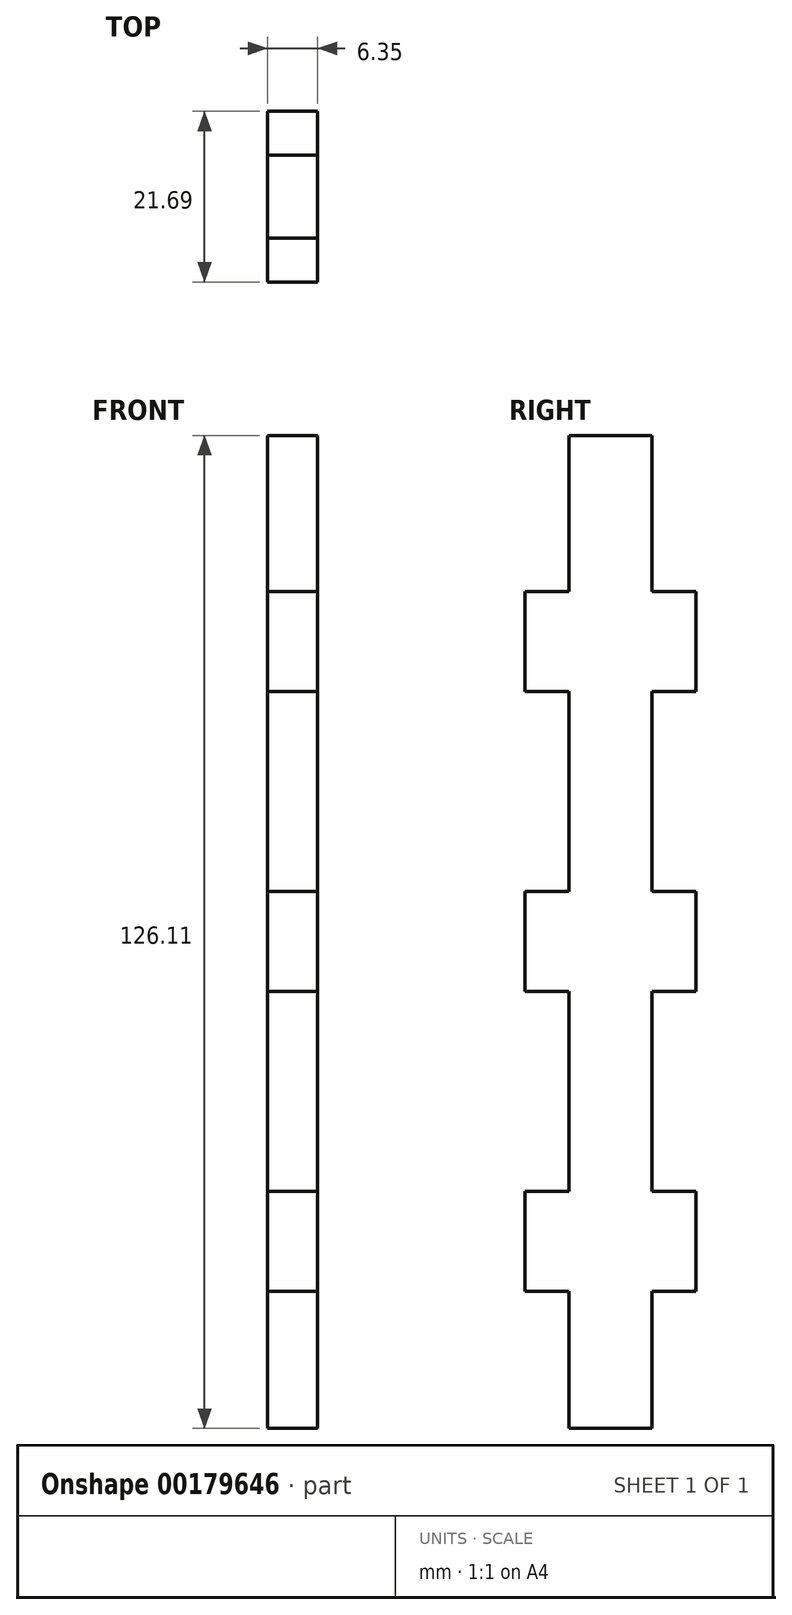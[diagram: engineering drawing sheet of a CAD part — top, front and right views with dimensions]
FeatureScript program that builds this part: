
annotation { "Feature Type Name" : "Feature", "Feature Type Description" : "" }
export const myFeature = defineFeature(function(context is Context, id is Id, definition is map)
    precondition{}
    {
        {
            var Q0;
            Q0=qCreatedBy(makeId("Right.planeOp"),FACE);
            var sketch = newSketch(context, id + "F0", { "sketchPlane" : qUnion([Q0])});
            skLineSegment(sketch, "E0.bottom", {"start": v(-44.05, 64.26) * mm, "end": v(-33.54, 64.26) * mm});
            skLineSegment(sketch, "E0.top", {"start": v(-44.05, -61.85) * mm, "end": v(-33.54, -61.85) * mm});
            skLineSegment(sketch, "E0.left", {"start": v(-49.64, 44.45) * mm, "end": v(-49.64, 31.75) * mm});
            skLineSegment(sketch, "E0.right", {"start": v(-27.95, 44.45) * mm, "end": v(-27.95, 31.75) * mm});
            skLineSegment(sketch, "E1", {"start": v(-33.54, 64.26) * mm, "end": v(-33.54, 44.45) * mm});
            skLineSegment(sketch, "E2", {"start": v(-33.54, 44.45) * mm, "end": v(-27.95, 44.45) * mm});
            skLineSegment(sketch, "E3", {"start": v(-27.95, 31.75) * mm, "end": v(-33.54, 31.75) * mm});
            skLineSegment(sketch, "E4", {"start": v(-33.54, 31.75) * mm, "end": v(-33.54, 6.35) * mm});
            skLineSegment(sketch, "E5", {"start": v(-33.54, 6.35) * mm, "end": v(-27.95, 6.35) * mm});
            skLineSegment(sketch, "E6", {"start": v(-27.95, 6.35) * mm, "end": v(-27.95, -6.35) * mm});
            skLineSegment(sketch, "E7", {"start": v(-27.95, -6.35) * mm, "end": v(-33.54, -6.35) * mm});
            skLineSegment(sketch, "E8", {"start": v(-33.54, -6.35) * mm, "end": v(-33.54, -31.75) * mm});
            skLineSegment(sketch, "E9", {"start": v(-33.54, -31.75) * mm, "end": v(-27.95, -31.75) * mm});
            skLineSegment(sketch, "E10", {"start": v(-27.95, -31.75) * mm, "end": v(-27.95, -44.45) * mm});
            skLineSegment(sketch, "E11", {"start": v(-27.95, -44.45) * mm, "end": v(-33.54, -44.45) * mm});
            skLineSegment(sketch, "E12", {"start": v(-33.54, -44.45) * mm, "end": v(-33.54, -61.85) * mm});
            skLineSegment(sketch, "E13.MirrorCS", {"start": v(-44.05, 64.26) * mm, "end": v(-44.05, 44.45) * mm});
            skLineSegment(sketch, "E14.MirrorCS", {"start": v(-44.05, 44.45) * mm, "end": v(-49.64, 44.45) * mm});
            skLineSegment(sketch, "E15.MirrorCS", {"start": v(-49.64, 31.75) * mm, "end": v(-44.05, 31.75) * mm});
            skLineSegment(sketch, "E16.MirrorCS", {"start": v(-44.05, 6.35) * mm, "end": v(-49.64, 6.35) * mm});
            skLineSegment(sketch, "E17.MirrorCS", {"start": v(-49.64, 6.35) * mm, "end": v(-49.64, -6.35) * mm});
            skLineSegment(sketch, "E18.MirrorCS", {"start": v(-49.64, -6.35) * mm, "end": v(-44.05, -6.35) * mm});
            skLineSegment(sketch, "E19.MirrorCS", {"start": v(-44.05, -31.75) * mm, "end": v(-49.64, -31.75) * mm});
            skLineSegment(sketch, "E20.MirrorCS", {"start": v(-49.64, -31.75) * mm, "end": v(-49.64, -44.45) * mm});
            skLineSegment(sketch, "E21.MirrorCS", {"start": v(-49.64, -44.45) * mm, "end": v(-44.05, -44.45) * mm});
            skLineSegment(sketch, "E22", {"start": v(2.15, 67.96) * mm, "end": v(2.15, -68.48) * mm});
            skLineSegment(sketch, "E23", {"start": v(-27.95, 0) * mm, "end": v(30.72, 0) * mm, "construction": true});
            skLineSegment(sketch, "E24", {"start": v(-44.05, -44.45) * mm, "end": v(-44.05, -61.85) * mm});
            skLineSegment(sketch, "E25", {"start": v(-44.05, 31.75) * mm, "end": v(-44.05, 6.35) * mm});
            skLineSegment(sketch, "E26", {"start": v(-44.05, -6.35) * mm, "end": v(-44.05, -31.75) * mm});
            skSolve(sketch);
        }
        {
            var Q0;
            Q0=makeQuery(id+"F0.imprint","IMPRINT",FACE,{"disambiguationData":[TD([[makeQuery(id+"F0.imprint","IMPRINT",EDGE,{"derivedFrom":sQuery(id+"F0.wireOp",EDGE,"E0.bottom")}),-1.0]])]});
            extrude(context, id + "F1", {"entities" : qUnion([Q0]), "depth" : 6.35 * mm});
        }
    });
